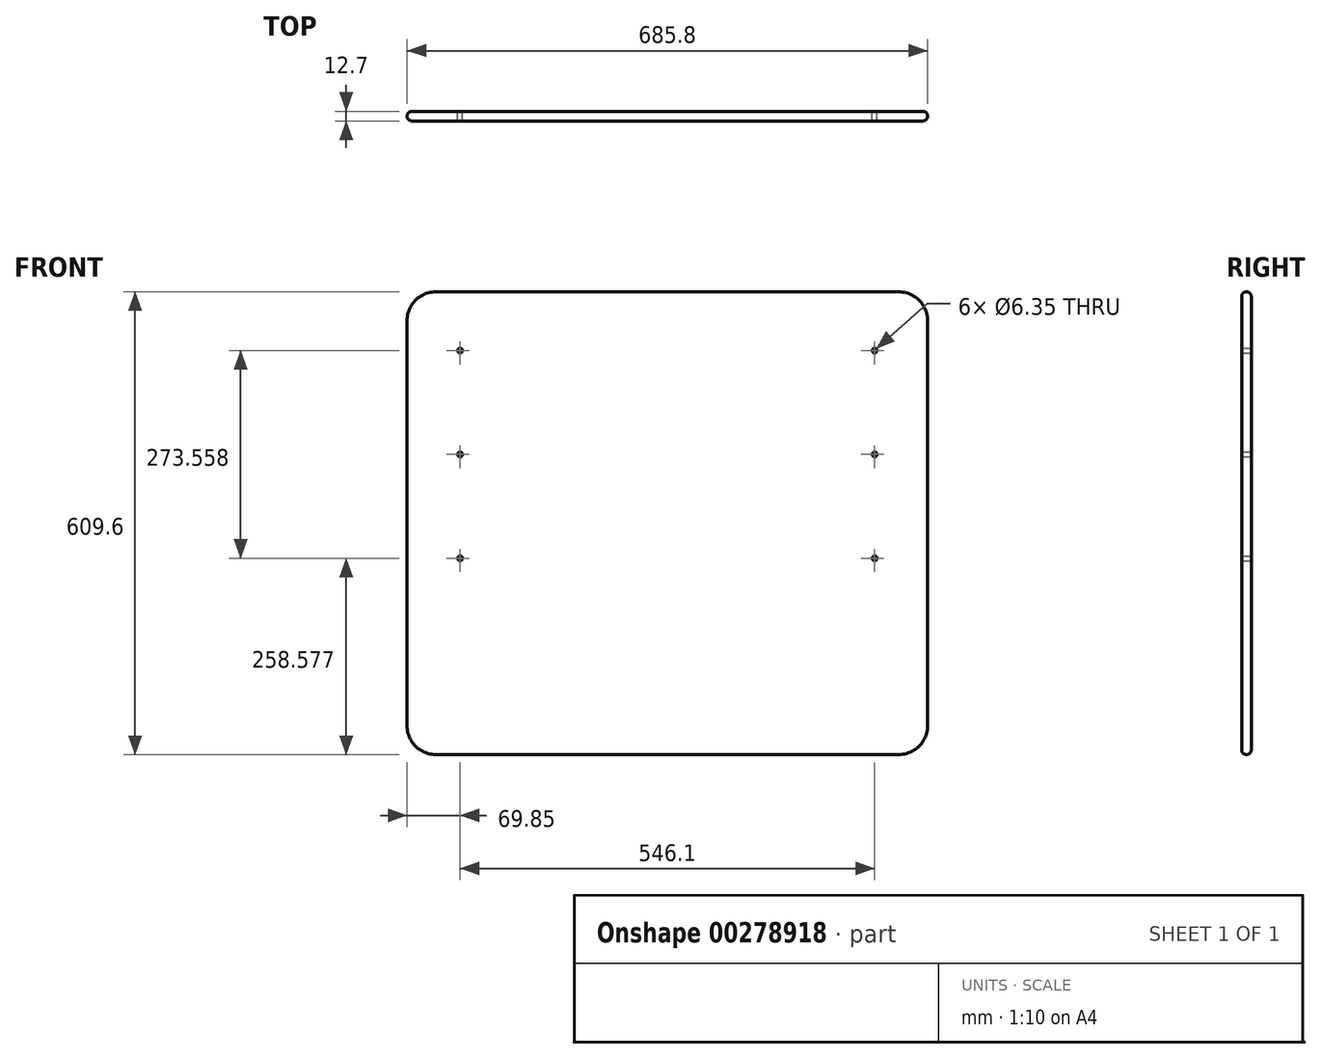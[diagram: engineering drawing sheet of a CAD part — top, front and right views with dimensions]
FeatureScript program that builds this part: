
annotation { "Feature Type Name" : "Feature", "Feature Type Description" : "" }
export const myFeature = defineFeature(function(context is Context, id is Id, definition is map)
    precondition{}
    {
        {
            var Q0;
            Q0=qCreatedBy(makeId("Front.planeOp"),FACE);
            var sketch = newSketch(context, id + "F0", { "sketchPlane" : qUnion([Q0])});
            skLineSegment(sketch, "E0.bottom", {"start": v(0, -166.26) * mm, "end": v(685.8, -166.26) * mm});
            skLineSegment(sketch, "E0.top", {"start": v(0, 443.34) * mm, "end": v(685.8, 443.34) * mm});
            skLineSegment(sketch, "E0.left", {"start": v(0, -166.26) * mm, "end": v(0, 443.34) * mm});
            skLineSegment(sketch, "E0.right", {"start": v(685.8, -166.26) * mm, "end": v(685.8, 443.34) * mm});
            skPoint(sketch, "E1", {"position": v(615.95, 365.87) * mm});
            skPoint(sketch, "E2", {"position": v(615.95, 229.22) * mm});
            skPoint(sketch, "E3", {"position": v(615.95, 92.32) * mm});
            skCircle(sketch, "E4", {"center": v(615.95, 365.87) * mm, "radius": 3.18 * mm});
            skCircle(sketch, "E5", {"center": v(615.95, 229.22) * mm, "radius": 3.18 * mm});
            skCircle(sketch, "E6", {"center": v(615.95, 92.32) * mm, "radius": 3.18 * mm});
            skCircle(sketch, "E7", {"center": v(69.85, 365.87) * mm, "radius": 3.18 * mm});
            skCircle(sketch, "E8", {"center": v(69.85, 229.22) * mm, "radius": 3.18 * mm});
            skCircle(sketch, "E9", {"center": v(69.85, 92.32) * mm, "radius": 3.18 * mm});
            skSolve(sketch);
        }
        {
            var Q0;
            Q0=qSketchRegion(id+"F0",true);
            extrude(context, id + "F3", {"entities" : qUnion([Q0]), "depth" : 12.7 * mm});
        }
        {
            var Q0;
            Q0=makeQuery(id+"F3.opExtrude","SWEPT_EDGE",EDGE,{"disambiguationData":[OSD([sQuery(id+"F0.wireOp",EDGE,"E0.bottom"),sQuery(id+"F0.wireOp",EDGE,"E0.left")])]});
            var Q1;
            Q1=makeQuery(id+"F3.opExtrude","SWEPT_EDGE",EDGE,{"disambiguationData":[OSD([sQuery(id+"F0.wireOp",EDGE,"E0.top"),sQuery(id+"F0.wireOp",EDGE,"E0.left")])]});
            var Q2;
            Q2=makeQuery(id+"F3.opExtrude","SWEPT_EDGE",EDGE,{"disambiguationData":[OSD([sQuery(id+"F0.wireOp",EDGE,"E0.top"),sQuery(id+"F0.wireOp",EDGE,"E0.right")])]});
            var Q3;
            Q3=makeQuery(id+"F3.opExtrude","SWEPT_EDGE",EDGE,{"disambiguationData":[OSD([sQuery(id+"F0.wireOp",EDGE,"E0.bottom"),sQuery(id+"F0.wireOp",EDGE,"E0.right")])]});
            fillet(context, id + "F1", {"entities" : qUnion([Q0, Q1, Q2, Q3]), "radius" : 38.1 * mm, "allowEdgeOverflow" : false});
        }
        {
            var Q0;
            Q0=makeQuery(id+"F3.opExtrude","CAP_EDGE",EDGE,{"disambiguationData":[OSD([sQuery(id+"F0.wireOp",EDGE,"E0.top")])],"isStart":false});
            var Q1;
            {var subQ0=sQuery(id+"F0.wireOp",EDGE,"E0.left");var subQ1=sQuery(id+"F0.wireOp",EDGE,"E0.bottom");Q1=makeQuery(id+"F1.opFillet","BLEND_EDGE",EDGE,{"blendedFrom":[makeQuery(id+"F3.opExtrude","SWEPT_EDGE",EDGE,{"disambiguationData":[OSD([subQ1,subQ0])]}),makeQuery(id+"F3.opExtrude","CAP_FACE",FACE,{"disambiguationData":[OSD([subQ1,sQuery(id+"F0.wireOp",EDGE,"E0.top"),subQ0,sQuery(id+"F0.wireOp",EDGE,"E0.right"),sQuery(id+"F0.wireOp",EDGE,"E4"),sQuery(id+"F0.wireOp",EDGE,"E5"),sQuery(id+"F0.wireOp",EDGE,"E6")])],"isStart":true})],"blendedInto":[makeQuery(id+"F3.opExtrude","CAP_FACE",FACE,{"disambiguationData":[OSD([subQ1,sQuery(id+"F0.wireOp",EDGE,"E0.top"),subQ0,sQuery(id+"F0.wireOp",EDGE,"E0.right"),sQuery(id+"F0.wireOp",EDGE,"E4"),sQuery(id+"F0.wireOp",EDGE,"E5"),sQuery(id+"F0.wireOp",EDGE,"E6")])],"isStart":true})]});}
            fillet(context, id + "F2", {"entities" : qUnion([Q0, Q1]), "radius" : 6.35 * mm, "tangentPropagation" : true, "allowEdgeOverflow" : false});
        }
    });
